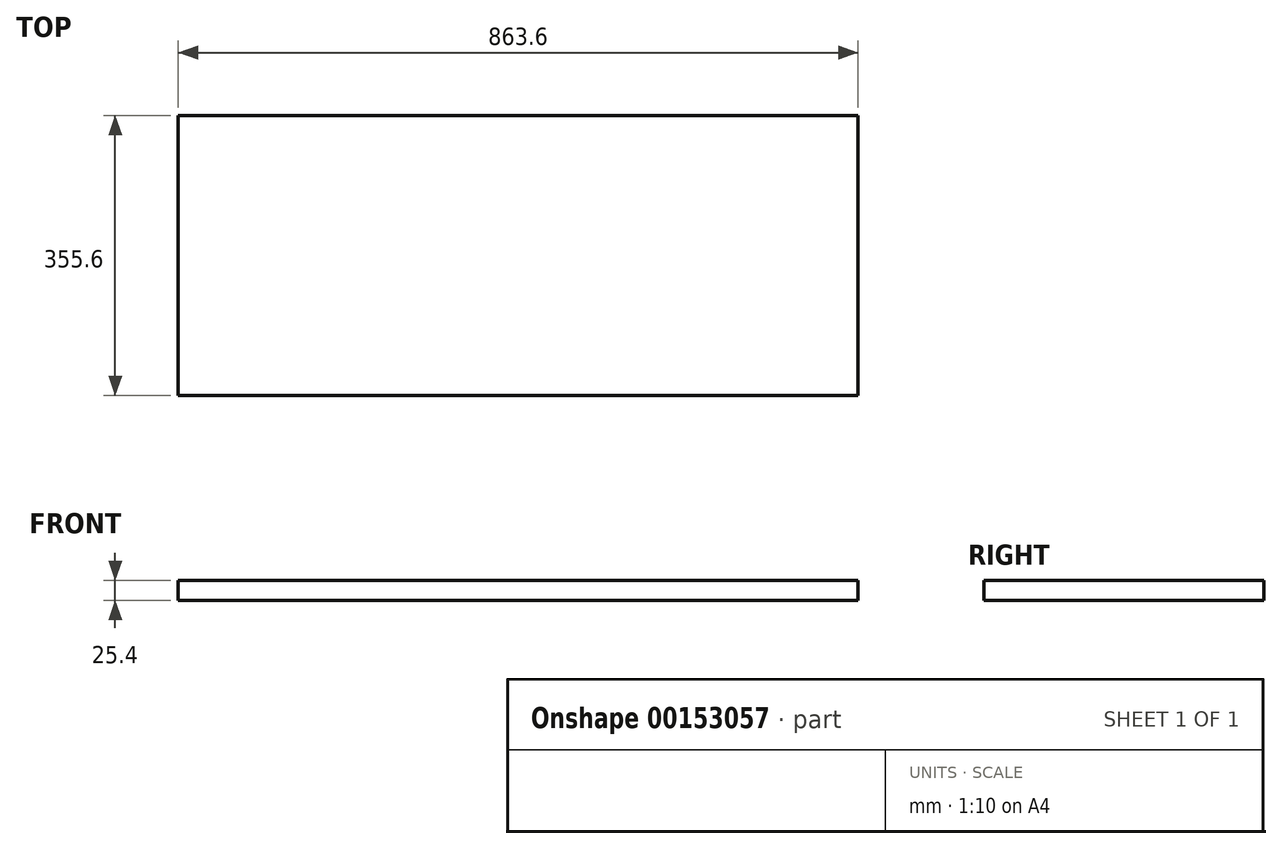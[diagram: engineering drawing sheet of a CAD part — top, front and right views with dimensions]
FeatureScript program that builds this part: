
annotation { "Feature Type Name" : "Feature", "Feature Type Description" : "" }
export const myFeature = defineFeature(function(context is Context, id is Id, definition is map)
    precondition{}
    {
        {
            var Q0;
            Q0=qCreatedBy(makeId("Top.planeOp"),FACE);
            var sketch = newSketch(context, id + "F0", { "sketchPlane" : qUnion([Q0])});
            skLineSegment(sketch, "E0.bottom", {"start": v(0, 0) * mm, "end": v(863.6, 0) * mm});
            skLineSegment(sketch, "E0.top", {"start": v(0, 355.6) * mm, "end": v(863.6, 355.6) * mm});
            skLineSegment(sketch, "E0.left", {"start": v(0, 0) * mm, "end": v(0, 355.6) * mm});
            skLineSegment(sketch, "E0.right", {"start": v(863.6, 0) * mm, "end": v(863.6, 355.6) * mm});
            skSolve(sketch);
        }
        {
            var Q0;
            Q0=makeQuery(id+"F0.imprint","IMPRINT",FACE,{"disambiguationData":[TD([[makeQuery(id+"F0.imprint","IMPRINT",EDGE,{"derivedFrom":sQuery(id+"F0.wireOp",EDGE,"E0.bottom")}),1.0]])]});
            extrude(context, id + "F1", {"entities" : qUnion([Q0]), "depth" : 25.4 * mm});
        }
    });
